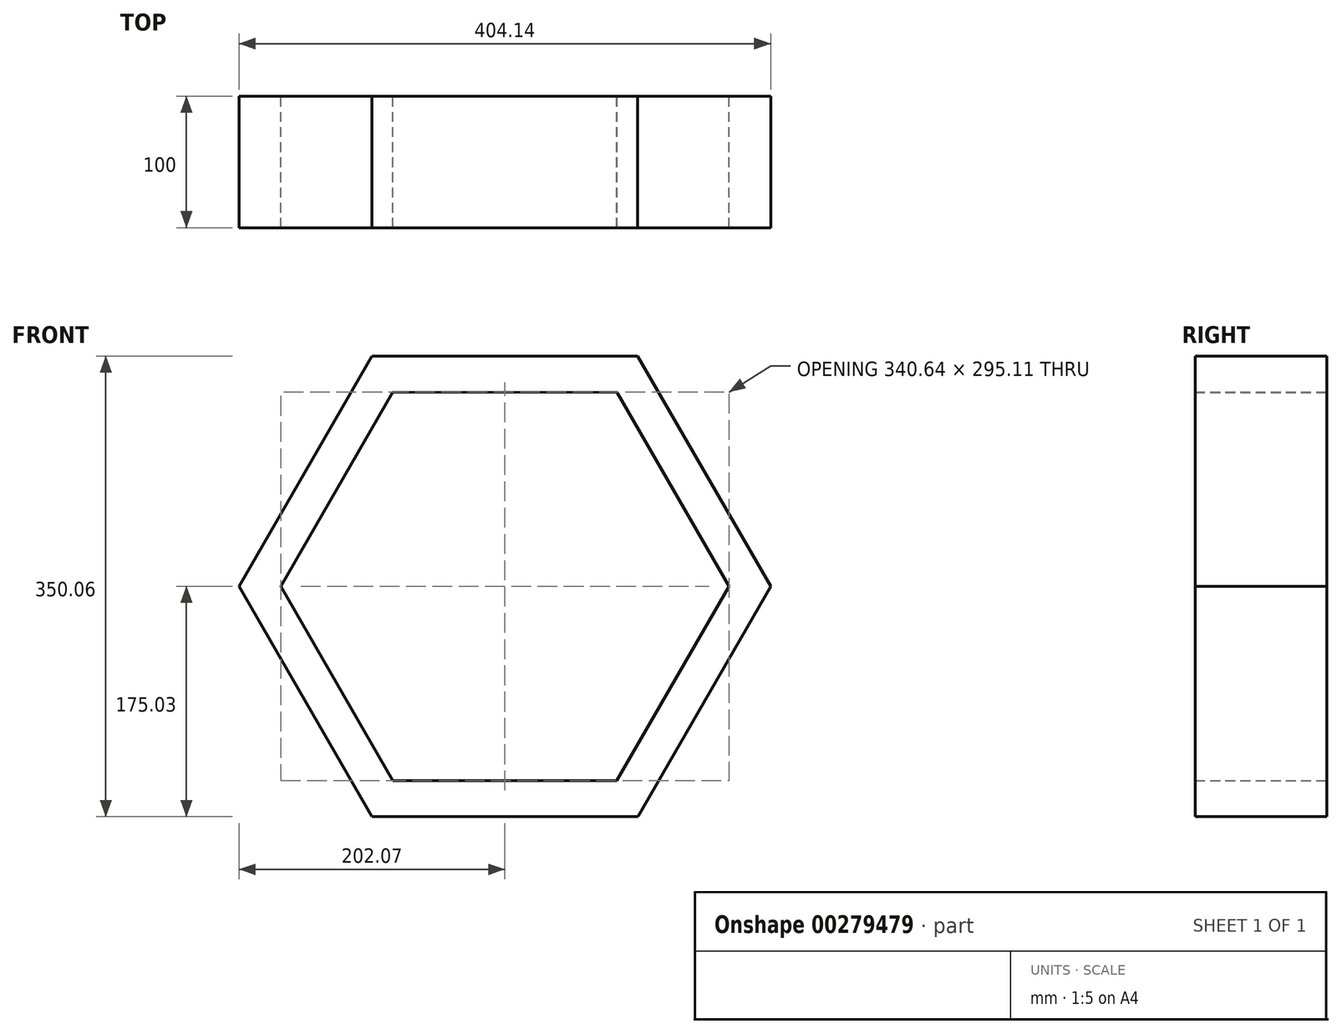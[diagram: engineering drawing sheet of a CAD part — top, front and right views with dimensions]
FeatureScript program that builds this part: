
annotation { "Feature Type Name" : "Feature", "Feature Type Description" : "" }
export const myFeature = defineFeature(function(context is Context, id is Id, definition is map)
    precondition{}
    {
        {
            var Q0;
            Q0=qCreatedBy(makeId("Front.planeOp"),FACE);
            var sketch = newSketch(context, id + "F0", { "sketchPlane" : qUnion([Q0])});
            skCircle(sketch, "E0.cCircle", {"center": v(0, 0) * mm, "radius": 175 * mm, "construction": true});
            skLineSegment(sketch, "E0.0", {"start": v(-101, -175.03) * mm, "end": v(-202.07, -0.05) * mm});
            skLineSegment(sketch, "E0.1", {"start": v(-202.07, -0.05) * mm, "end": v(-101.08, 174.97) * mm});
            skLineSegment(sketch, "E0.2", {"start": v(-101.08, 174.97) * mm, "end": v(101, 175.03) * mm});
            skLineSegment(sketch, "E0.3", {"start": v(101, 175.03) * mm, "end": v(202.07, 0.05) * mm});
            skLineSegment(sketch, "E0.4", {"start": v(202.07, 0.05) * mm, "end": v(101.08, -174.97) * mm});
            skLineSegment(sketch, "E0.5", {"start": v(101.08, -174.97) * mm, "end": v(-101, -175.03) * mm});
            skPoint(sketch, "E0.0.midPoint", {"position": v(-151.53, -87.54) * mm});
            skSolve(sketch);
        }
        {
            var Q0;
            Q0=makeQuery(id+"F0.imprint","IMPRINT",FACE,{"disambiguationData":[TD([[makeQuery(id+"F0.imprint","IMPRINT",EDGE,{"derivedFrom":sQuery(id+"F0.wireOp",EDGE,"E0.0")}),-1.0]])]});
            var sketch = newSketch(context, id + "F1", { "sketchPlane" : qUnion([Q0])});
            skCircle(sketch, "E1.cCircle", {"center": v(0, 0) * mm, "radius": 147.5 * mm, "construction": true});
            skLineSegment(sketch, "E1.0", {"start": v(-85.26, -147.44) * mm, "end": v(-170.32, 0.11) * mm});
            skLineSegment(sketch, "E1.1", {"start": v(-170.32, 0.11) * mm, "end": v(-85.06, 147.56) * mm});
            skLineSegment(sketch, "E1.2", {"start": v(-85.06, 147.56) * mm, "end": v(85.26, 147.44) * mm});
            skLineSegment(sketch, "E1.3", {"start": v(85.26, 147.44) * mm, "end": v(170.32, -0.11) * mm});
            skLineSegment(sketch, "E1.4", {"start": v(170.32, -0.11) * mm, "end": v(85.06, -147.56) * mm});
            skLineSegment(sketch, "E1.5", {"start": v(85.06, -147.56) * mm, "end": v(-85.26, -147.44) * mm});
            skPoint(sketch, "E1.0.midPoint", {"position": v(-127.79, -73.67) * mm});
            skSolve(sketch);
        }
        {
            var Q0;
            Q0=makeQuery(id+"F0.imprint","IMPRINT",FACE,{"disambiguationData":[TD([[makeQuery(id+"F0.imprint","IMPRINT",EDGE,{"derivedFrom":sQuery(id+"F0.wireOp",EDGE,"E0.0")}),-1.0]])]});
            extrude(context, id + "F2", {"entities" : qUnion([Q0]), "depth" : 100 * mm, "offsetDistance" : 25 * mm});
        }
        {
            var Q0;
            Q0=makeQuery(id+"F1.imprint","IMPRINT",FACE,{"disambiguationData":[TD([[makeQuery(id+"F1.imprint","IMPRINT",EDGE,{"derivedFrom":sQuery(id+"F1.wireOp",EDGE,"E1.0")}),-1.0]])]});
            extrude(context, id + "F3", {"entities" : qUnion([Q0]), "operationType" : NewBodyOperationType.REMOVE, "depth" : 191 * mm, "offsetDistance" : 25 * mm});
        }
    });
